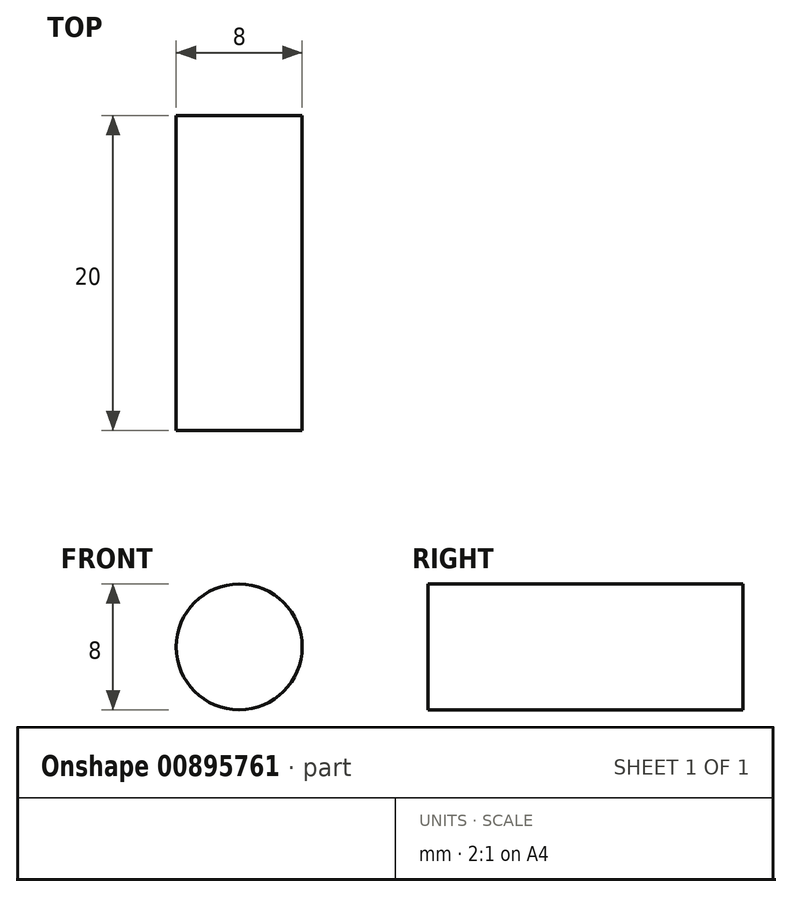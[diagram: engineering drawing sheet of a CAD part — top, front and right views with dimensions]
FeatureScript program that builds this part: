
annotation { "Feature Type Name" : "Feature", "Feature Type Description" : "" }
export const myFeature = defineFeature(function(context is Context, id is Id, definition is map)
    precondition{}
    {
        {
            var Q0;
            Q0=qCreatedBy(makeId("Front.planeOp"),FACE);
            var sketch = newSketch(context, id + "F0", { "sketchPlane" : qUnion([Q0])});
            skCircle(sketch, "E0", {"center": v(0, 0) * mm, "radius": 4 * mm});
            skSolve(sketch);
        }
        {
            var Q0;
            Q0=makeQuery(id+"F0.imprint","IMPRINT",FACE,{"disambiguationData":[TD([[makeQuery(id+"F0.imprint","IMPRINT",EDGE,{"derivedFrom":sQuery(id+"F0.wireOp",EDGE,"E0")}),1.0]])]});
            var Q1;
            Q1=sQuery(id+"F0.wireOp",EDGE,"E0");
            extrude(context, id + "F1", {"entities" : qUnion([Q0]), "surfaceEntities" : qUnion([Q1]), "offsetDistance" : 25 * mm, "depth" : 17 * mm});
        }
        {
            var Q0;
            Q0=makeQuery(id+"F1.opExtrude","CAP_FACE",FACE,{"disambiguationData":[OSD([sQuery(id+"F0.wireOp",EDGE,"E0")])],"isStart":false});
            extrude(context, id + "F2", {"entities" : qUnion([Q0]), "operationType" : NewBodyOperationType.ADD, "depth" : 3 * mm});
        }
    });
